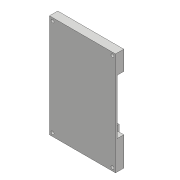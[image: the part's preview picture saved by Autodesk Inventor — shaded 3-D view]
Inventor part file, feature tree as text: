
AUTODESK INVENTOR PART (.ipt)
format: ipt  version: 2018 (Build 220112000, 112)  size: 140,800 bytes
history: native  units: mm
features: sketch x6, extrude x5, hole x1
ambient origin geometry x8: Origin, YZ Plane, XZ Plane, XY Plane, X Axis, Y Axis, Z Axis, Center Point
bodies: Solid1 (feature_tree)
feature tree (12):
  extrude  "Extrusion1"  Depth=68.59mm
  extrude  "Extrusion2"  Depth=20.0mm
  extrude  "Extrusion3"  Depth=7.0mm TaperAngle=0.0deg
  extrude  "Extrusion4"  Depth=16.0mm
  hole  "Hole1"  [1 undecoded]
  extrude  "Extrusion5"  Depth=7.0mm TaperAngle=0.0deg
  sketch  "Sketch1"  dims[d0=106.92mm d1=68.59mm]
  sketch  "Sketch2"  dims[d2=1.6mm d3=0.0mm d4=20.0mm]
  sketch  "Sketch3"  dims[d5=30.0mm d6=7.0mm d7=0.0mm]
  sketch  "Sketch4"  dims[d8=19.93mm d9=16.0mm]
  sketch  "Sketch5"  dims[d10=7.0mm d11=0.0mm d12=12.0mm]
  sketch  "Sketch6"  dims[d13=10.0mm d14=7.0mm d15=0.0mm d16=3.18mm d17=3.18mm d18=3.18mm d19=3.3mm d20=3.2mm d21=6.0mm d22=6.3mm d23=2.0mm d24=90.0deg d25=8.0mm d26=20.594885mm d27=24.0mm d28=24.0mm d29=6.0mm d30=3.0mm d31=0.0mm]
note: 1 required parameter value undecoded (feature->parameter linkage not recoverable at this tier; creation-order binding heuristic only, values carry confidence <= 0.55)
